# Revit family: Hager-WITTY ONE ON PEDESTAL-de-AT-AT
name_source: partatom
category: Electrical Fixtures
units: mm (PartAtom-declared; Revit-internal decimal feet)

## family parameters
Always vertical = Yes
Cut with Voids When Loaded = No
Maintain Annotation Orientation = No
Part Type = Normal
Room Calculation Point = No
Round Connector Dimension = Use Diameter
Shared = No
Work Plane-Based = No

## types (8) — shared parameters
BC_METADATA = {"ObjectGuid":"309c69a2-f6b5-4723-8d44-322179afe64e","ModelGuid":"04826155-e6fb-4358-826f-cf700e871803","VariantGuid":"d0dc6e8a-84e1-41b3-adf0-62c97217fd0d","Revision":"#2","VariantName":"REF 1"}
BC_MODEL_ID = 1528342
BC_OBJECT_ID = 511099
BC_OBJECT_VERSION = #1
Code hager = ADD_EC002883_ECVS_WO
EF000003 - Montageart = Wandmontage
EF000008 - Breite = 250 mm  [stored 0.82021 ft]
EF000040 - Höhe = 370 mm  [stored 1.21391 ft]
EF000049 - Tiefe = 150 mm
EF000458 - Mit Display = No
EF001596 - Werkstoff des Gehäuses = Kunststoff
EF004293 - Schlagfestigkeit = IK08
EF005455 - Frequenz = 50/60 Hz
EF005474 - Schutzart (IP) = IP54
EF007001 - Ausgangsspannung DC = 0 V
EF007353 - Max. Ausgangsstrom DC = 0 A
EF009078 - Anzahl der Ladepunkte = 1
EF009089 - Mit Hausanschlusskasten (HAK) = No
EF009305 - Anzahl der Ladesteckdosen Typ 2 = 1
EF009313 - Mit Energiezähler = No
EF009314 - Mit Leitungsschutzschalter = No
EF009547 - LTE = No
EF011072 - IFTTT-Unterstützung verfügbar = No
EF012191 - Mit integriertem RFID-Kartenleser = Yes
EF012361 - NFC (Near Field Communication) = No
EF013154 - Vernetzbar über WLAN = No
EF014925 - Kompatibel mit Apple HomeKit = No
EF014926 - Kompatibel mit Google Assistant = No
EF014927 - Kompatibel mit Amazon Alexa = No
EF016385 - Mobilfunkstandard 5G = No
EF017508 - Vernetzbar als Master = No
EF017509 - DC-Fehlerstromerkennung = Yes
EF017510 - Schützkontakt-Verschweiß-Erkennung = Yes
EF017511 - Mit Schlüsselschalter = No
EF017513 - Open Charge Point Protocol (OCPP) Version = 1.6
EF017515 - Plug and charge (ISO 15118) = No
EF017517 - Vernetzbar als Extender = No
EF017663 - Ladekabel dauerhaft verriegelbar an der Ladestation = Yes
EF017664 - Vernetzbar über LAN = No
EF017665 - Mit MID-kompatiblem Energiezähler = No
EF017668 - Statisches Lastmanagement integriert = No
EF017669 - Geeignet für dynamisches Lastmanagement = Yes
EF017672 - Backend mitgeliefert = No
EF017972 - Bedienung und Konfiguration über App = Yes
EFDE0066 - Eichrechtskonform = No
ETIM class code = EC002883
ETIM class name = Charging device E-Mobility
HG000003-Range = WITTY ONE
HG000065-With socket TE = No
HG000099-Onfly Template ID = WittyOne_EVCS_On_Pedestal
Manufacturer = hager France
Name = WITTY ONE ON PEDESTAL-AT
Name BIM&CO = Electricity
Name hager = ADD_ChargingStation_EC002883
zero-valued in all types: Default Elevation, EF006577 - Anzahl der CEE-Steckdosen (IEC 60309), EF008200 - Anschließbarer Leiterquerschnitt, EF009091 - Anzahl der FI-Schalter Typ A, EF009092 - Anzahl der FI-Schalter Typ B, EF009301 - Anzahl der Ladekupplungen Typ 1, EF009302 - Anzahl der Ladekupplungen Typ 1 CCS, EF009303 - Anzahl der Ladekupplungen Typ 2, EF009304 - Anzahl der Ladekupplungen Typ 2 CCS, EF009306 - Anzahl der Ladekupplungen GB AC, EF009307 - Anzahl der Ladekupplungen GB DC, EF009308 - Anzahl der Ladesteckdosen GB, EF009309 - Anzahl der Ladesteckdosen Typ 3, EF009310 - Anzahl der Ladekupplungen CHAdeMO, EF009311 - Anzahl der Haushaltssteckdosen

## per-type parameters (varying)
| type | BC_VARIANT_ID | EF002136 - Nennanschlussleistung | EF003840 - Eingangsspannung | EF009300 - Max. Leistung pro Ladepunkt | EF014895 - Länge des Ladekabels | EF017512 - Export der Ladehistorie | EF025053 - Ausführung Anschluss Anlagenseite | HG000004-Manufacturer reference | Reference description |
| WITTY ONE-1x7kW-1P-XVR107C-DOUBLE STATION-RECTANGULAR PEDESTAL | 1164384 | 7000 W | 230 V | 7000 W | 6500 mm  [stored 21.3255 ft] | No | 1-phasig | XVR107C / XVR107C / XVA135 | ECVS Witty 1x7kW 1P T2S |
| WITTY ONE-1x7kW-1P-XVR107C-RECTANGULAR PEDESTAL | 1164385 | 7000 W | 230 V | 7000 W | 6500 mm  [stored 21.3255 ft] | No | 1-phasig | XVR107C / XVA130 | ECVS Witty 1x7kW 1P T2S |
| WITTY ONE-1x11kW-3P-XVR111S-RECTANGULAR PEDESTAL | 1164386 | 11000 W | 400 V | 11000 W | 0 mm  [stored 0 ft] | Yes | 3-phasig | XVR111S / XVA130 | ECVS Witty 1x11kW 3P T2S |
| WITTY ONE-1x11kW-3P-XVR111S-DOUBLE STATION-RECTANGULAR PEDESTAL | 1164387 | 11000 W | 400 V | 11000 W | 0 mm  [stored 0 ft] | Yes | 3-phasig | XVR111S / XVR111S / XVA135 | ECVS Witty 1x11kW 3P T2S |
| WITTY ONE-1x7kW-1P-XVR107S-DOUBLE STATION-RECTANGULAR PEDESTAL | 1164388 | 7000 W | 230 V | 7000 W | 0 mm  [stored 0 ft] | Yes | 1-phasig | XVR107S / XVR107S / XVA135 | ECVS Witty 1x7kW 1P T2S |
| WITTY ONE-1x7kW-1P-XVR107S-RECTANGULAR PEDESTAL | 1164389 | 7000 W | 230 V | 7000 W | 0 mm  [stored 0 ft] | Yes | 1-phasig | XVR107S / XVA130 | ECVS Witty 1x7kW 1P T2S |
| WITTY ONE-1x11kW-3P-XVR111C-DOUBLE STATION-RECTANGULAR PEDESTAL | 1164390 | 11000 W | 400 V | 11000 W | 6500 mm  [stored 21.3255 ft] | Yes | 3-phasig | XVR111C / XVR111C / XVA135 | ECVS Witty 1x11kW 3P T2S |
| WITTY ONE-1x11kW-3P-XVR111C-RECTANGULAR PEDESTAL | 1164391 | 11000 W | 400 V | 11000 W | 6500 mm  [stored 21.3255 ft] | Yes | 3-phasig | XVR111C / XVA130 | ECVS Witty 1x11kW 3P T2S |

note: column(s) folded — value = type name in every type: Reference

note: [stored X ft] marks values corroborated as IEEE doubles in the binary element streams (Revit-internal decimal feet)
